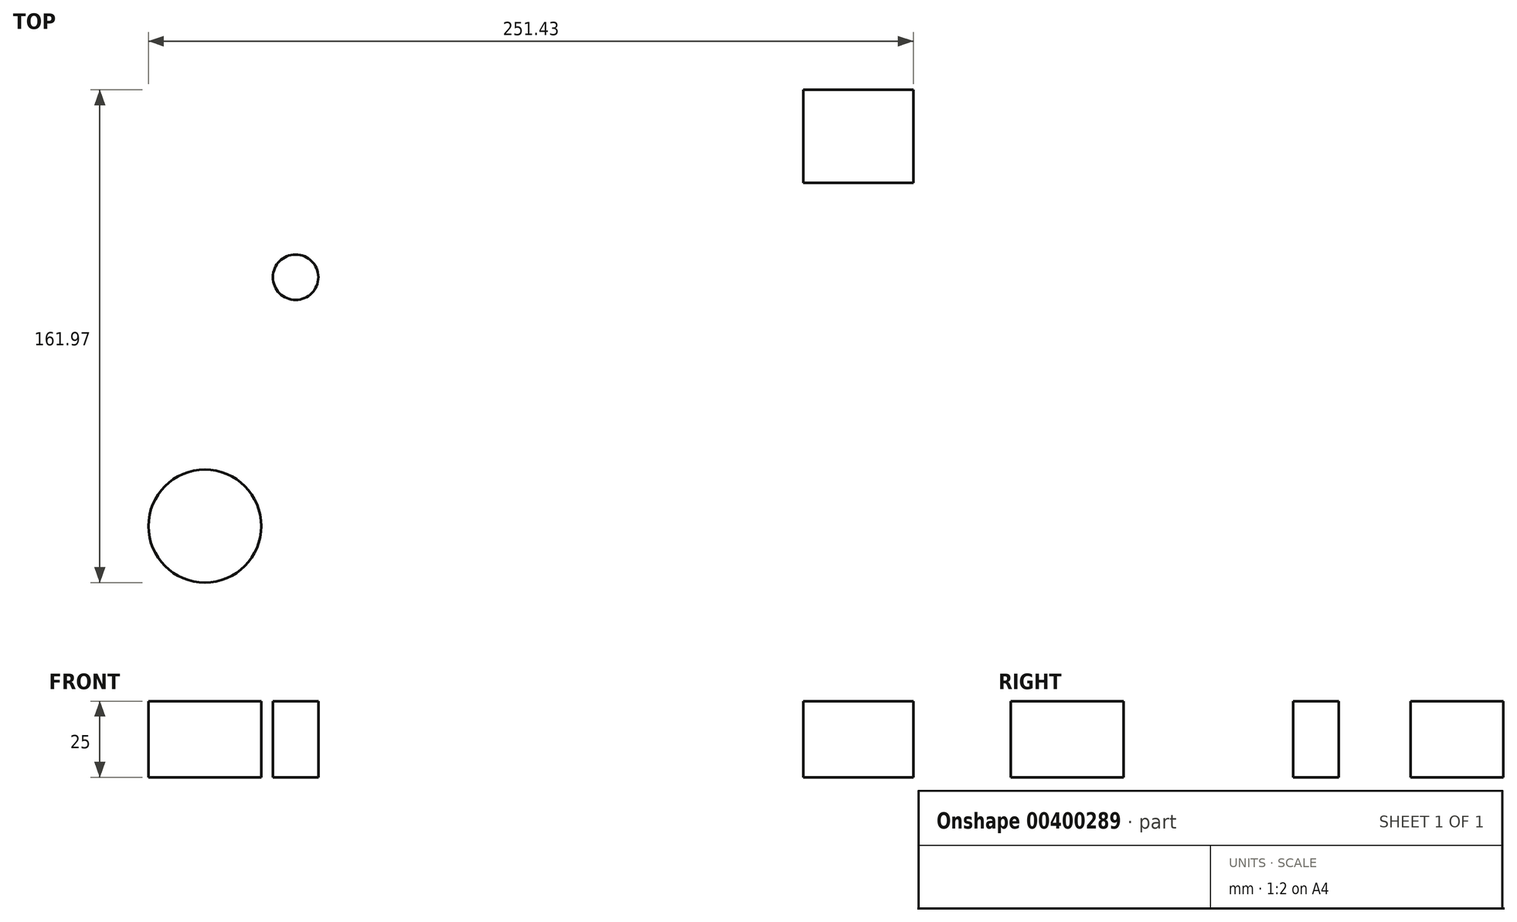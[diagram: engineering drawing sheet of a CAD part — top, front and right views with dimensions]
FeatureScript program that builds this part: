
annotation { "Feature Type Name" : "Feature", "Feature Type Description" : "" }
export const myFeature = defineFeature(function(context is Context, id is Id, definition is map)
    precondition{}
    {
        {
            var Q0;
            Q0=qCreatedBy(makeId("Top.planeOp"),FACE);
            var sketch = newSketch(context, id + "F0", { "sketchPlane" : qUnion([Q0])});
            skLineSegment(sketch, "E0", {"start": v(-196.74, -143.41) * mm, "end": v(-223.7, -38.53) * mm});
            skCircle(sketch, "E1", {"center": v(-196.74, -143.41) * mm, "radius": 18.55 * mm});
            skCircle(sketch, "E2", {"center": v(-166.92, -61.6) * mm, "radius": 7.47 * mm});
            skFitSpline(sketch, "E3", {"points": [v(-223.7, -38.53) * mm, v(-235.74, -40.87) * mm, v(-239.8, -38.53) * mm, v(-235.76, -27.12) * mm, v(-229.54, -25.4) * mm, v(-214.3, -29.88) * mm, v(-220.55, -38.53) * mm, v(-220.02, -31.48) * mm, v(-223.7, -34.98) * mm, v(-228.8, -30.42) * mm, v(-236.04, -36.53) * mm, v(-226.94, -35.7) * mm, v(-229.31, -32.62) * mm], "startDerivative": vector(-129.37, -35.61) * mm, "endDerivative": vector(-83.77, 56.07) * mm});
            skLineSegment(sketch, "E4.bottom", {"start": v(0, 0) * mm, "end": v(36.14, 0) * mm});
            skLineSegment(sketch, "E4.top", {"start": v(0, -30.54) * mm, "end": v(36.14, -30.54) * mm});
            skLineSegment(sketch, "E4.left", {"start": v(0, 0) * mm, "end": v(0, -30.54) * mm});
            skLineSegment(sketch, "E4.right", {"start": v(36.14, 0) * mm, "end": v(36.14, -30.54) * mm});
            skSolve(sketch);
        }
        {
            var Q0;
            Q0 = qSketchRegion(id + "F0", true);
            extrude(context, id + "F1", {"entities" : qUnion([Q0]), "depth" : 25 * mm});
        }
    });
